# Revit family: P710080-031-30
name_source: partatom
category: Lighting Fixtures
revit_build: Autodesk Revit 2014 (Build: 20130308_1515(x64)
units: mm (PartAtom-declared; Revit-internal decimal feet)

## types (1)
- P710080-031-30
    Apparent Load = 10 VA
    Assembly Code = D5020200
    Color Filter = 16777215
    Connector Description = Lighting Connector
    Default Elevation = 48 "
    Depth = 3.25 "
    Description = The organic features of this wall sconce make it seem like it’s one with nature.
The handmade, clear stone glass shade steals the show with its underwater-inspired ambiance. The shade is held in place by a minimalist black frame
that transforms your home into a naturally beautiful soothing place for you
and your family.
    Dimming Lamp Color Temperature Shift = <None>
    Features = Clear Stone glass Square Panel
• The organic features of this wall sconce make it seem like it’s one with nature.
• The handmade, clear stone glass shade steals the show with its underwater-inspired ambiance.
• The shade is held in place by a minimalist black frame that transforms your home into a
naturally beautiful soothing place for you and your family.
• Ideal for bedroom, hallway, foyer, bathroom, or living room.
• Perfect for transitional, modern, or contemporary settings.
• Measures 8-inch width by 8-1/2-inch height.
• Uses one integrated LED (9.5w max).
• Compatible with many Triac dimmers (see dimming controls)
• Includes installation instructions and mounting hardware.
• Progress Lighting products are designed for exceptional quality, reliability, and functionality.
• Dimmable to 10% brightness (See Dimming Notes)
• Canopy covers a standard 4” recessed outlet box: 8 in W., 4.75 in ht., 0.75 in depth
• Mounting backplate for outlet box included
• 6 in of wire supplied
• Americans With Disabilities Act (ADA) compliant
    Fixture distribution = Direct
    Glass = Hubbell - Glass
    HeightLength = 8.5 "
    Housing Material = Paint - Hubbell - Basic Black Textured
    Lamp = LED
    Load Classification = Lighting
    Manufacturer = Progress Lighting
    Model = P710080-031-30
    Mounting = Paint - Hubbell - Light Silver
    Photometric Web File = PROG_P710080-031-30_19.01537_testlabreports.ies
    Power Factor = 1
    Product Documentation Link = https://hubbellcdn.com
    Product Link = https://www.hubbell.com
    Reflector Finish = Hubbell - White Glass
    Tilt Angle = -90.00°
    URL = https://www.hubbell.com
    Voltage = 120 V
    Warranty = 5 years Warranty
    Wattage Comments = 10W
    Watts = 10 W
    Width = 8 "
    Wings = Paint - Hubbell - Light Silver

## geometry (parser evidence)
native form markers: Sweep x4
no freeform markers — native parametric forms only
